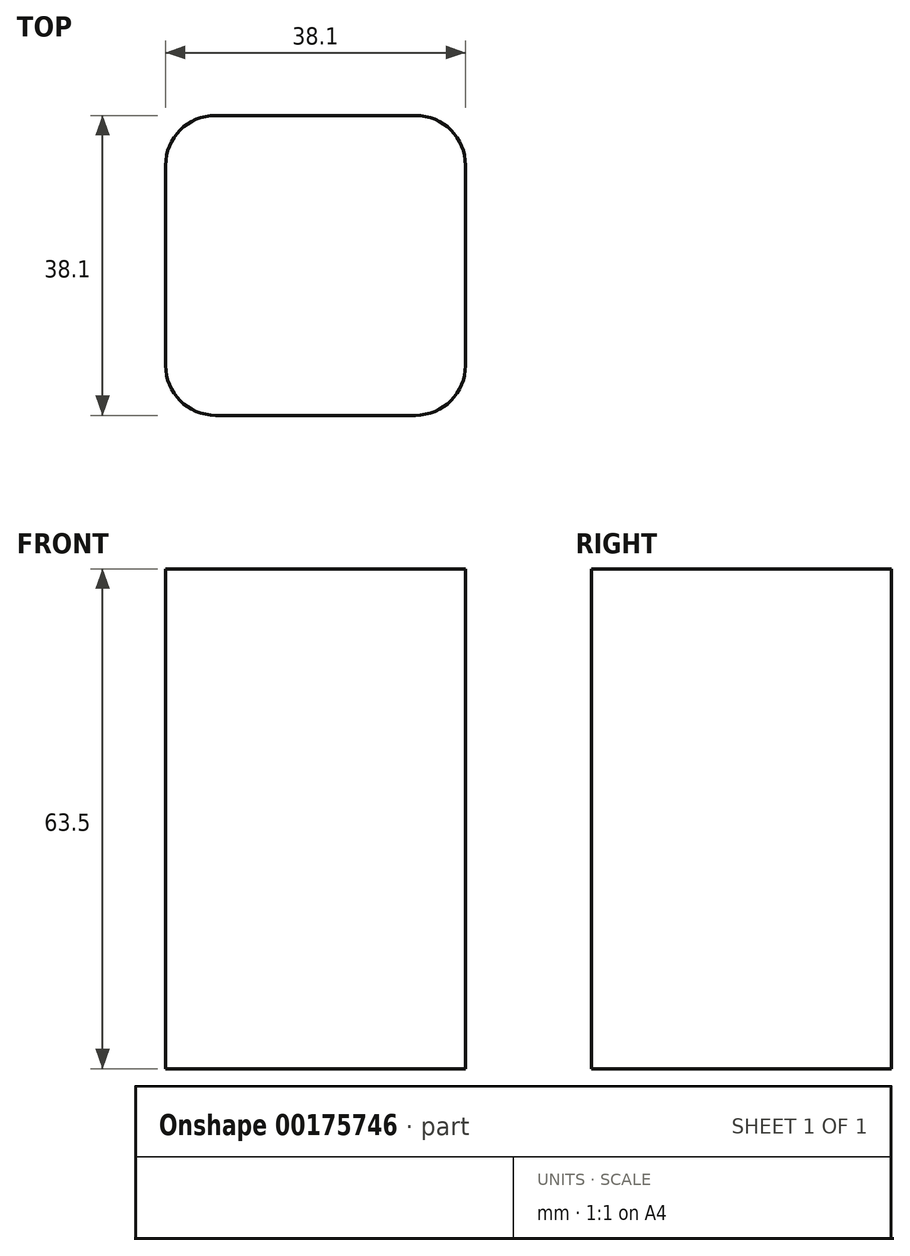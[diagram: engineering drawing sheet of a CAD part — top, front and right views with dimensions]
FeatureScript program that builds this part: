
annotation { "Feature Type Name" : "Feature", "Feature Type Description" : "" }
export const myFeature = defineFeature(function(context is Context, id is Id, definition is map)
    precondition{}
    {
        {
            var Q0;
            Q0=qCreatedBy(makeId("Top.planeOp"),FACE);
            var sketch = newSketch(context, id + "F0", { "sketchPlane" : qUnion([Q0])});
            skLineSegment(sketch, "E0.bottom", {"start": v(12.7, 19.05) * mm, "end": v(-12.7, 19.05) * mm});
            skLineSegment(sketch, "E0.top", {"start": v(12.7, -19.05) * mm, "end": v(-12.7, -19.05) * mm});
            skLineSegment(sketch, "E0.left", {"start": v(19.05, 12.7) * mm, "end": v(19.05, -12.7) * mm});
            skLineSegment(sketch, "E0.right", {"start": v(-19.05, 12.7) * mm, "end": v(-19.05, -12.7) * mm});
            skPoint(sketch, "E0.middle", {"position": v(0, 0) * mm});
            skPoint(sketch, "E1.visualSharp", {"position": v(-19.05, 19.05) * mm});
            skArc(sketch, "E1.filletArc", {"start": v(-12.7, 19.05) * mm, "mid": v(-17.2, 17.2) * mm, "end": v(-19.05, 12.7) * mm});
            skPoint(sketch, "E2.visualSharp", {"position": v(19.05, 19.05) * mm});
            skArc(sketch, "E2.filletArc", {"start": v(19.05, 12.7) * mm, "mid": v(17.2, 17.2) * mm, "end": v(12.7, 19.05) * mm});
            skPoint(sketch, "E3.visualSharp", {"position": v(19.05, -19.05) * mm});
            skArc(sketch, "E3.filletArc", {"start": v(12.7, -19.05) * mm, "mid": v(17.2, -17.2) * mm, "end": v(19.05, -12.7) * mm});
            skPoint(sketch, "E4.visualSharp", {"position": v(-19.05, -19.05) * mm});
            skArc(sketch, "E4.filletArc", {"start": v(-19.05, -12.7) * mm, "mid": v(-17.2, -17.2) * mm, "end": v(-12.7, -19.05) * mm});
            skSolve(sketch);
        }
        {
            var Q0;
            Q0=qSketchRegion(id+"F0",true);
            extrude(context, id + "F1", {"entities" : qUnion([Q0]), "depth" : 63.5 * mm, "offsetDistance" : 25.4 * mm});
        }
        {
            var Q0;
            Q0=qCreatedBy(makeId("Right.planeOp"),FACE);
            var sketch = newSketch(context, id + "F2", { "sketchPlane" : qUnion([Q0])});
            skLineSegment(sketch, "E5.bottom", {"start": v(-186.2, -72.65) * mm, "end": v(-198.9, -72.65) * mm});
            skLineSegment(sketch, "E5.top", {"start": v(-186.2, 117.85) * mm, "end": v(-198.9, 117.85) * mm});
            skLineSegment(sketch, "E5.left", {"start": v(-186.2, -72.65) * mm, "end": v(-186.2, 117.85) * mm});
            skLineSegment(sketch, "E5.right", {"start": v(-198.9, -72.65) * mm, "end": v(-198.9, 117.85) * mm});
            skPoint(sketch, "E5.middle", {"position": v(-192.55, 22.6) * mm});
            skSolve(sketch);
        }
        {
            var Q0;
            Q0=qCreatedBy(makeId("Right.planeOp"),FACE);
            var sketch = newSketch(context, id + "F3", { "sketchPlane" : qUnion([Q0])});
            skLineSegment(sketch, "E6.bottom", {"start": v(182.21, -70.47) * mm, "end": v(169.51, -70.47) * mm});
            skLineSegment(sketch, "E6.top", {"start": v(182.21, 120.03) * mm, "end": v(169.51, 120.03) * mm});
            skLineSegment(sketch, "E6.left", {"start": v(182.21, -70.47) * mm, "end": v(182.21, 120.03) * mm});
            skLineSegment(sketch, "E6.right", {"start": v(169.51, -70.47) * mm, "end": v(169.51, 120.03) * mm});
            skPoint(sketch, "E6.middle", {"position": v(175.86, 24.78) * mm});
            skSolve(sketch);
        }
        {
            var Q0;
            Q0=makeQuery(id+"F2.imprint","IMPRINT",FACE,{"disambiguationData":[TD([[makeQuery(id+"F2.imprint","IMPRINT",EDGE,{"derivedFrom":sQuery(id+"F2.wireOp",EDGE,"E5.bottom")}),-1.0]])]});
            extrude(context, id + "F4", {"entities" : qUnion([Q0]), "depth" : 0.25 * mm});
        }
        {
            var Q0;
            Q0=makeQuery(id+"F3.imprint","IMPRINT",FACE,{"disambiguationData":[TD([[makeQuery(id+"F3.imprint","IMPRINT",EDGE,{"derivedFrom":sQuery(id+"F3.wireOp",EDGE,"E6.bottom")}),-1.0]])]});
            extrude(context, id + "F5", {"entities" : qUnion([Q0]), "depth" : 0.25 * mm});
        }
        {
            var Q0;
            Q0=makeQuery(id+"F4.opExtrude","SWEPT_BODY",BODY,{"disambiguationData":[OSD([sQuery(id+"F2.wireOp",EDGE,"E5.bottom"),sQuery(id+"F2.wireOp",EDGE,"E5.top"),sQuery(id+"F2.wireOp",EDGE,"E5.left"),sQuery(id+"F2.wireOp",EDGE,"E5.right")])]});
            var Q1;
            Q1=makeQuery(id+"F5.opExtrude","SWEPT_BODY",BODY,{"disambiguationData":[OSD([sQuery(id+"F3.wireOp",EDGE,"E6.bottom"),sQuery(id+"F3.wireOp",EDGE,"E6.top"),sQuery(id+"F3.wireOp",EDGE,"E6.left"),sQuery(id+"F3.wireOp",EDGE,"E6.right")])]});
            deleteBodies(context, id + "F6", {"entities" : qUnion([Q0, Q1])});
        }
    });
